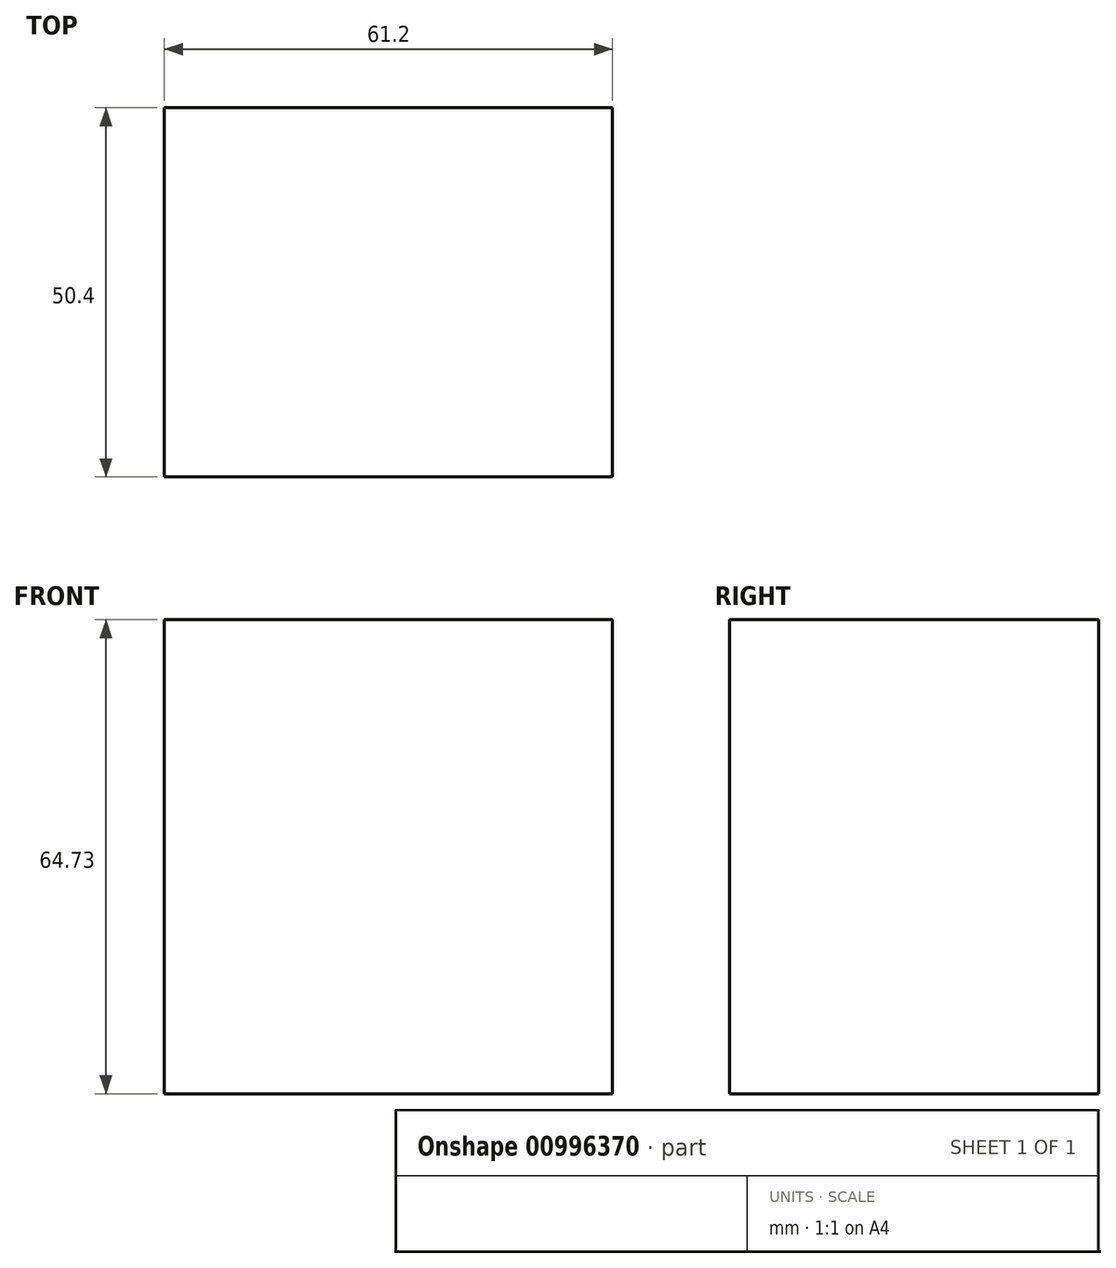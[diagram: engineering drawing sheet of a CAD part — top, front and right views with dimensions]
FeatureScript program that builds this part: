
annotation { "Feature Type Name" : "Feature", "Feature Type Description" : "" }
export const myFeature = defineFeature(function(context is Context, id is Id, definition is map)
    precondition{}
    {
        {
            var Q0;
            Q0=qCreatedBy(makeId("Front.planeOp"),FACE);
            var sketch = newSketch(context, id + "F0", { "sketchPlane" : qUnion([Q0])});
            skLineSegment(sketch, "E0.bottom", {"start": v(-30.08, 41.08) * mm, "end": v(31.12, 41.08) * mm});
            skLineSegment(sketch, "E0.top", {"start": v(-30.08, -23.65) * mm, "end": v(31.12, -23.65) * mm});
            skLineSegment(sketch, "E0.left", {"start": v(-30.08, 41.08) * mm, "end": v(-30.08, -23.65) * mm});
            skLineSegment(sketch, "E0.right", {"start": v(31.12, 41.08) * mm, "end": v(31.12, -23.65) * mm});
            skSolve(sketch);
        }
        {
            var Q0;
            Q0=makeQuery(id+"F0.imprint","IMPRINT",FACE,{"disambiguationData":[TD([[makeQuery(id+"F0.imprint","IMPRINT",EDGE,{"derivedFrom":sQuery(id+"F0.wireOp",EDGE,"E0.bottom")}),-1.0]])]});
            extrude(context, id + "F1", {"entities" : qUnion([Q0]), "depth" : 50.4 * mm, "offsetDistance" : 25.4 * mm});
        }
    });
